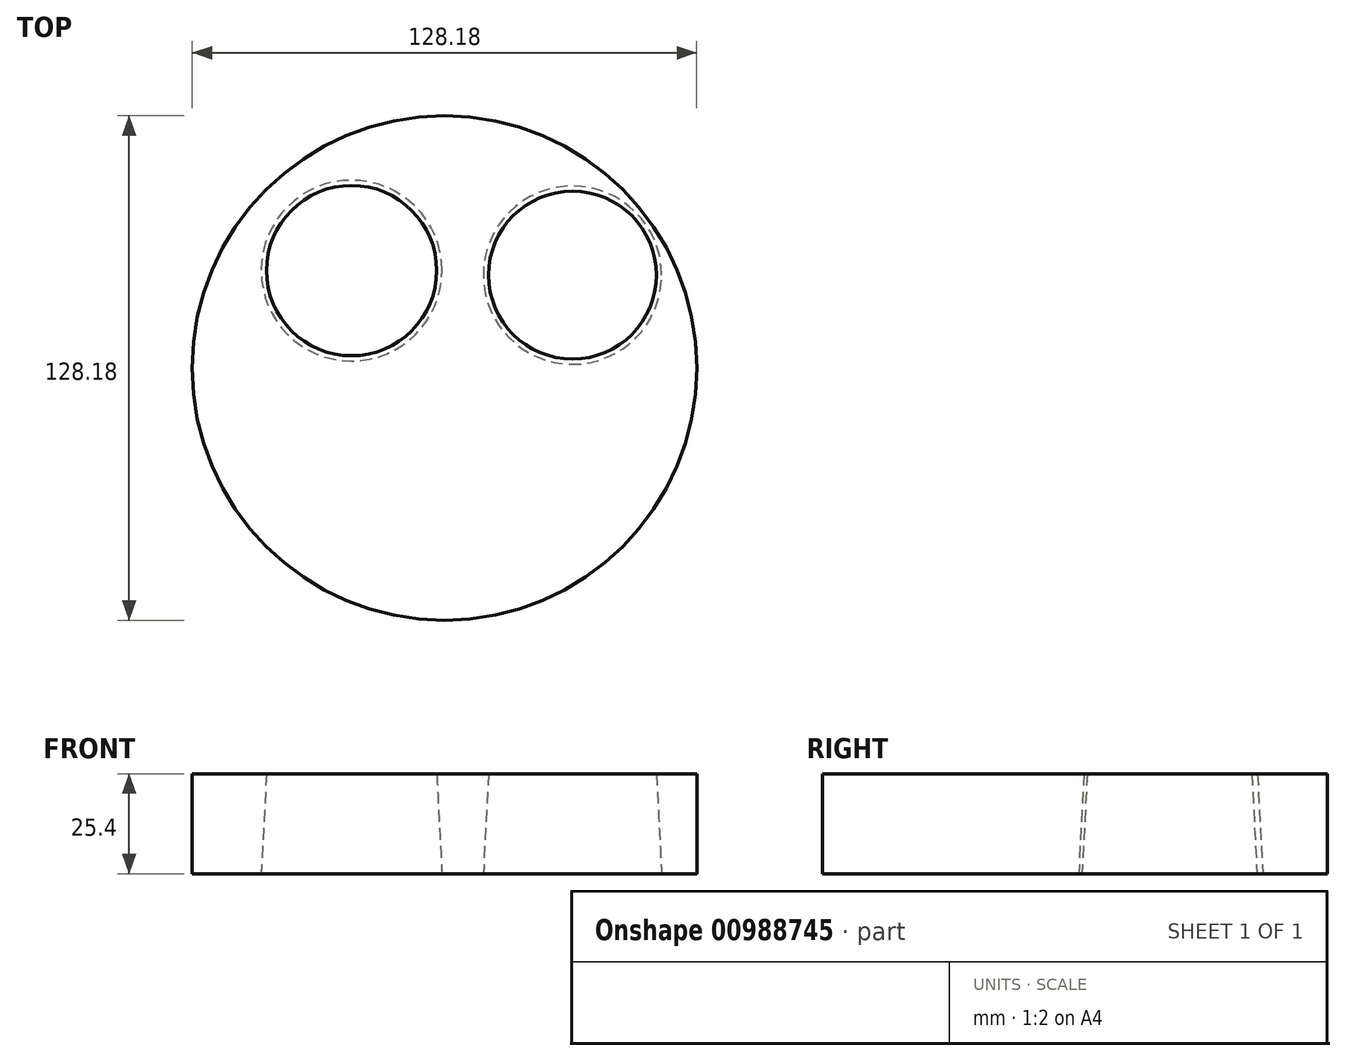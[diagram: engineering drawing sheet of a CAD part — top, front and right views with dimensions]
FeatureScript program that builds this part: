
annotation { "Feature Type Name" : "Feature", "Feature Type Description" : "" }
export const myFeature = defineFeature(function(context is Context, id is Id, definition is map)
    precondition{}
    {
        {
            var Q0;
            Q0=qCreatedBy(makeId("Top.planeOp"),FACE);
            var sketch = newSketch(context, id + "F0", { "sketchPlane" : qUnion([Q0])});
            skCircle(sketch, "E0", {"center": v(-4.75, 3.3) * mm, "radius": 64.1 * mm});
            skSolve(sketch);
        }
        {
            var Q0;
            Q0=makeQuery(id+"F0.imprint","IMPRINT",FACE,{"disambiguationData":[TD([[makeQuery(id+"F0.imprint","IMPRINT",EDGE,{"derivedFrom":sQuery(id+"F0.wireOp",EDGE,"E0")}),1.0]])]});
            extrude(context, id + "F1", {"entities" : qUnion([Q0]), "depth" : 25.4 * mm, "offsetDistance" : 25.4 * mm});
        }
        {
            var Q0;
            Q0=makeQuery(id+"F1.opExtrude","CAP_FACE",FACE,{"disambiguationData":[OSD([sQuery(id+"F0.wireOp",EDGE,"E0")])],"isStart":false});
            var sketch = newSketch(context, id + "F2", { "sketchPlane" : qUnion([Q0])});
            skCircle(sketch, "E1", {"center": v(-28.35, 28.06) * mm, "radius": 21.63 * mm});
            skCircle(sketch, "E2", {"center": v(27.77, 26.9) * mm, "radius": 21.32 * mm});
            skSolve(sketch);
        }
        {
            var Q0;
            Q0 = qSketchRegion(id + "F2", true);
            extrude(context, id + "F3", {"entities" : qUnion([Q0]), "operationType" : NewBodyOperationType.REMOVE, "oppositeDirection" : true, "depth" : 25.4 * mm, "offsetDistance" : 25.4 * mm, "hasDraft" : true, "draftAngle" : 3 * degree});
        }
    });
